# Revit family: TD92_BEL056_TRA011_RVT20_R00
name_source: partatom
category: Mobiliário
units: mm (PartAtom-declared; Revit-internal decimal feet)

## family parameters
Com base no plano de trabalho = Não
Compartilhado = Não
Corte com vazios quando carregada = Não
Número OmniClass = 23.40.20.00
Ponto de cálculo do ambiente = Não
Sempre na vertical = Sim
Título OmniClass = General Furniture and Specialties

## types (1)
- TD92_BEL056_TRA011_RVT20_R00
    Descrição = Inspirada na elegância e estilo das cadeiras do século passado, a Belle Époque retrata os minuciosos detalhes que enriquecem e enobrecem a peça tornando-a sinônimo de imponência e estilo. A Cadeira Tramontina Belle Époque em Policarbonato Preto faz parte da linha summa, é leve, resistente e com design diferenciado. Sua principal matéria prima é o policarbonato, aproximadamente 250 vezes mais resistente que o vidro.
    Elevação padrão = 0  [stored 0 ft]
    Fabricante = Tramontina Delta S/A
    Modelo = Cadeira Tramontina Belle Époque em Policarbonato Transparente
    Nota-chave = 92056011
    URL = https://www.tramontinastore.com

note: [stored X ft] marks values corroborated as IEEE doubles in the binary element streams (Revit-internal decimal feet)
